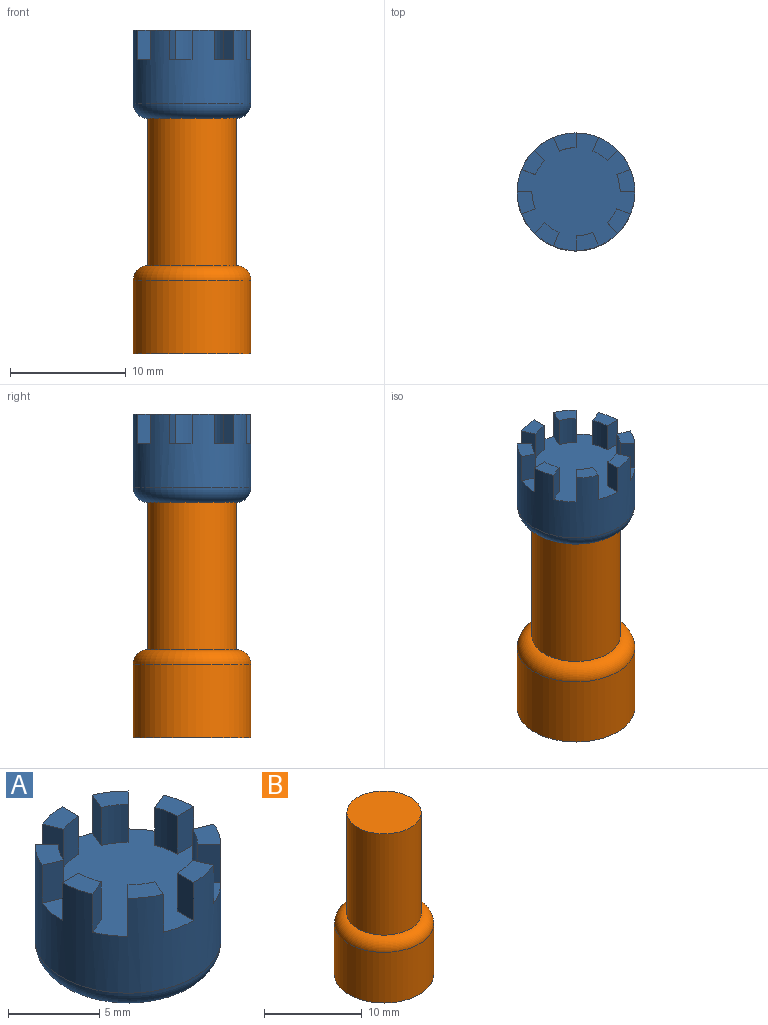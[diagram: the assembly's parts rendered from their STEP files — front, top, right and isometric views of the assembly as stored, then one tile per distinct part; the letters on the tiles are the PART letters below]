
ASSEMBLY  parts=2 mates=1
PART A: 36 faces, bbox 11x11x7.6 mm
  f0: cylinder r=5.08mm len=10.16mm, axis (0,0,-1), area 162.1mm2, adj f1,f3,f4,f6,f7,f8,f10,f11
  f1: plane 10.16x10.16mm, normal (0,0,1), area 63.3mm2, adj f0,f3,f4,f5,f7,f8,f9,f11
  f2: plane 7.62x7.62mm, normal (0,0,-1), area 45.6mm2, adj f35
  f3: plane 2.54x1.27mm, normal (0,-1,0), area 3.2mm2, adj f0,f1,f5,f6
  f4: plane 2.54x1.17mm, normal (-0.38,0.92,0), area 3.2mm2, adj f0,f1,f5,f6
  f5: cylinder r=3.81mm len=2.54mm, axis (0,0,-1), area 3.8mm2, adj f1,f3,f4,f6
  f6: plane 1.94x1.56mm, normal (0,0,1), area 2.2mm2, adj f0,f3,f4,f5
  f7: plane 2.54x1.17mm, normal (-0.92,0.38,0), area 3.2mm2, adj f0,f1,f9,f10
  f8: plane 2.54x0.9mm, normal (0.71,-0.71,0), area 3.2mm2, adj f0,f1,f9,f10
  f9: cylinder r=3.81mm len=2.54mm, axis (0,0,-1), area 3.8mm2, adj f1,f7,f8,f10
  f10: plane 2.13x2mm, normal (0,0,1), area 2.2mm2, adj f0,f7,f8,f9
  f11: plane 2.54x1.17mm, normal (-0.92,-0.38,0), area 3.2mm2, adj f0,f1,f13,f14
  f12: plane 2.54x1.27mm, normal (1,0,0), area 3.2mm2, adj f0,f1,f13,f14
  f13: cylinder r=3.81mm len=2.54mm, axis (0,0,-1), area 3.8mm2, adj f1,f11,f12,f14
  f14: plane 1.94x1.56mm, normal (0,0,1), area 2.2mm2, adj f0,f11,f12,f13
  f15: plane 2.54x1.17mm, normal (-0.38,-0.92,0), area 3.2mm2, adj f0,f1,f17,f18
  f16: plane 2.54x0.9mm, normal (0.71,0.71,0), area 3.2mm2, adj f0,f1,f17,f18
  f17: cylinder r=3.81mm len=2.54mm, axis (0,0,-1), area 3.8mm2, adj f1,f15,f16,f18
  f18: plane 2.13x2mm, normal (0,0,1), area 2.2mm2, adj f0,f15,f16,f17
  f19: plane 2.54x1.17mm, normal (0.38,-0.92,0), area 3.2mm2, adj f0,f1,f21,f22
  f20: plane 2.54x1.27mm, normal (0,1,0), area 3.2mm2, adj f0,f1,f21,f22
  f21: cylinder r=3.81mm len=2.54mm, axis (0,0,-1), area 3.8mm2, adj f1,f19,f20,f22
  f22: plane 1.94x1.56mm, normal (0,0,1), area 2.2mm2, adj f0,f19,f20,f21
  f23: plane 2.54x1.17mm, normal (0.92,-0.38,0), area 3.2mm2, adj f0,f1,f25,f26
  f24: plane 2.54x0.9mm, normal (-0.71,0.71,0), area 3.2mm2, adj f0,f1,f25,f26
  f25: cylinder r=3.81mm len=2.54mm, axis (0,0,-1), area 3.8mm2, adj f1,f23,f24,f26
  f26: plane 2.13x2mm, normal (0,0,1), area 2.2mm2, adj f0,f23,f24,f25
  f27: plane 2.54x1.17mm, normal (0.92,0.38,0), area 3.2mm2, adj f0,f1,f29,f30
  f28: plane 2.54x1.27mm, normal (-1,0,0), area 3.2mm2, adj f0,f1,f29,f30
  f29: cylinder r=3.81mm len=2.54mm, axis (0,0,-1), area 3.8mm2, adj f1,f27,f28,f30
  f30: plane 1.94x1.56mm, normal (0,0,1), area 2.2mm2, adj f0,f27,f28,f29
  f31: plane 2.54x0.9mm, normal (-0.71,-0.71,0), area 3.2mm2, adj f0,f1,f33,f34
  f32: plane 2.54x1.17mm, normal (0.38,0.92,0), area 3.2mm2, adj f0,f1,f33,f34
  f33: cylinder r=3.81mm len=2.54mm, axis (0,0,-1), area 3.8mm2, adj f1,f31,f32,f34
  f34: plane 2.13x2mm, normal (0,0,1), area 2.2mm2, adj f0,f31,f32,f33
  f35: torus R=3.81mm, axis (0,0,1), area 57.9mm2, adj f0,f2
PART B: 5 faces, bbox 11x11x20.3 mm
  f0: cylinder r=5.08mm len=10.16mm, axis (0,0,-1), area 202.7mm2, adj f1,f2
  f1: plane 10.16x10.16mm, normal (0,0,-1), area 81.1mm2, adj f0
  f2: torus R=3.81mm, axis (0,0,1), area 57.9mm2, adj f0,f3
  f3: cylinder r=3.81mm len=12.7mm, axis (0,0,-1), area 304mm2, adj f2,f4
  f4: plane 7.62x7.62mm, normal (0,0,1), area 45.6mm2, adj f3
PLACE A t=(0,0,20.32)mm
PLACE B at identity
MATE planar A.f0 <-> B.f0  axis (0,0,-1) through (0,0,20.32)mm
